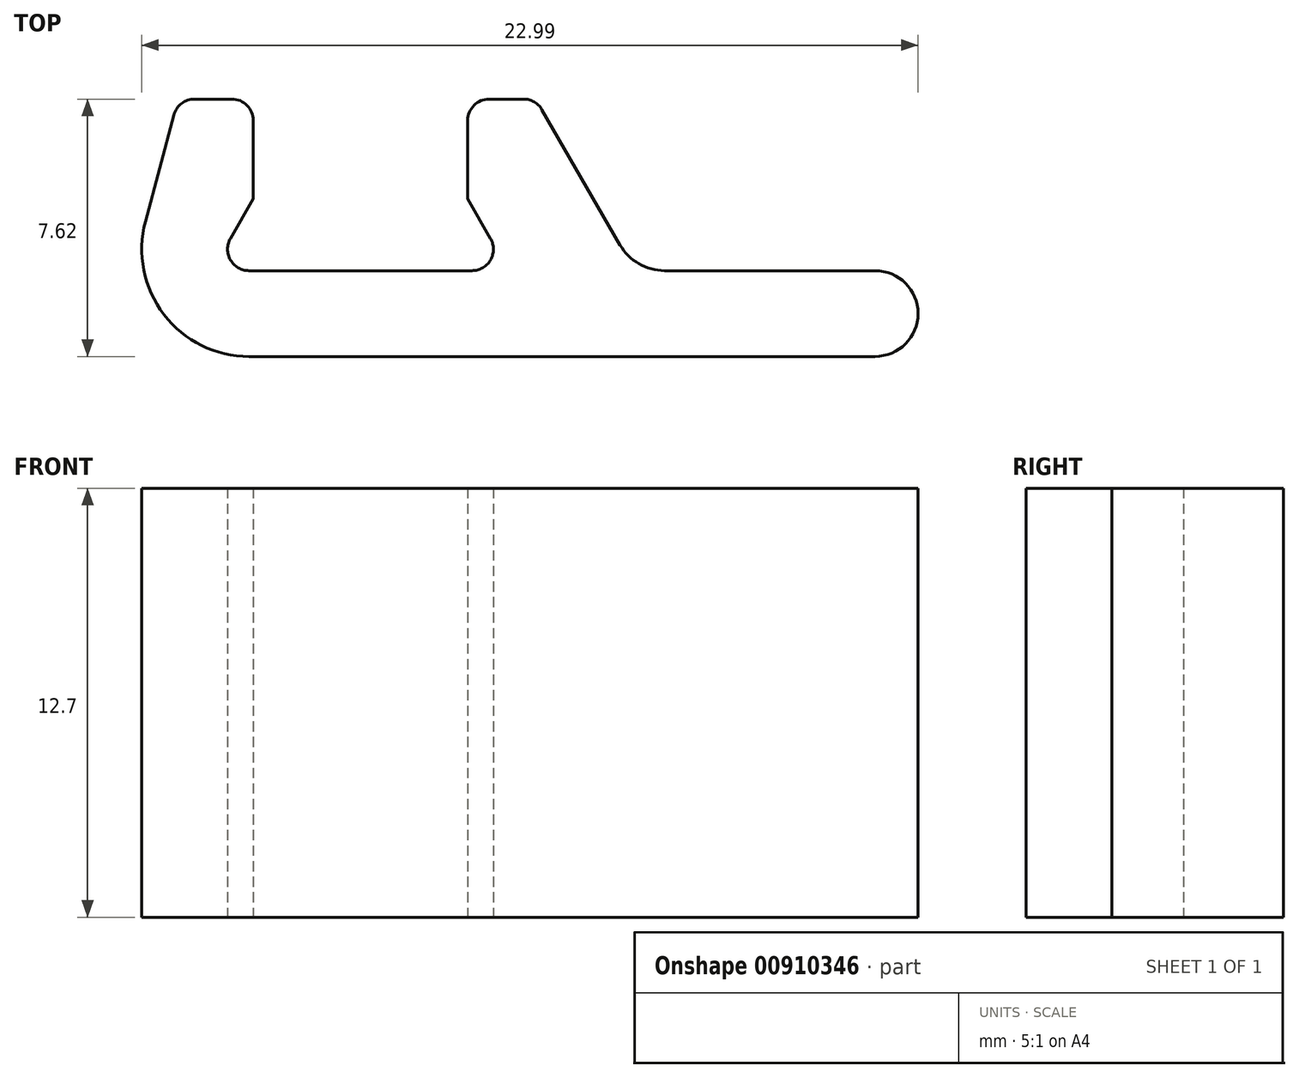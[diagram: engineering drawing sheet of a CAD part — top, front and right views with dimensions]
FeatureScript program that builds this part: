
annotation { "Feature Type Name" : "Feature", "Feature Type Description" : "" }
export const myFeature = defineFeature(function(context is Context, id is Id, definition is map)
    precondition{}
    {
        {
            var Q0;
            Q0=qCreatedBy(makeId("Top.planeOp"),FACE);
            var sketch = newSketch(context, id + "F0", { "sketchPlane" : qUnion([Q0])});
            skLineSegment(sketch, "E0", {"start": v(-3.3, 0) * mm, "end": v(3.3, 0) * mm});
            skLineSegment(sketch, "E1", {"start": v(-3.18, 2.12) * mm, "end": v(-3.18, 4.45) * mm});
            skLineSegment(sketch, "E2", {"start": v(-5.52, 4.6) * mm, "end": v(-6.37, 1.46) * mm});
            skLineSegment(sketch, "E3", {"start": v(3.18, 4.45) * mm, "end": v(3.18, 2.12) * mm});
            skLineSegment(sketch, "E4", {"start": v(-3.18, 2.12) * mm, "end": v(-3.85, 0.95) * mm});
            skLineSegment(sketch, "E5", {"start": v(3.18, 2.12) * mm, "end": v(3.85, 0.95) * mm});
            skArc(sketch, "E6", {"start": v(3.3, 0) * mm, "mid": v(3.85, 0.32) * mm, "end": v(3.85, 0.95) * mm});
            skArc(sketch, "E7", {"start": v(-3.85, 0.95) * mm, "mid": v(-3.85, 0.32) * mm, "end": v(-3.3, 0) * mm});
            skLineSegment(sketch, "E8", {"start": v(5.38, 4.76) * mm, "end": v(7.69, 0.76) * mm});
            skLineSegment(sketch, "E9", {"start": v(-4.91, 5.08) * mm, "end": v(-3.81, 5.08) * mm});
            skLineSegment(sketch, "E10", {"start": v(3.81, 5.08) * mm, "end": v(4.83, 5.08) * mm});
            skArc(sketch, "E11", {"start": v(-4.91, 5.08) * mm, "mid": v(-5.3, 4.95) * mm, "end": v(-5.52, 4.6) * mm});
            skArc(sketch, "E12", {"start": v(-3.18, 4.45) * mm, "mid": v(-3.36, 4.9) * mm, "end": v(-3.81, 5.08) * mm});
            skArc(sketch, "E13", {"start": v(3.81, 5.08) * mm, "mid": v(3.36, 4.9) * mm, "end": v(3.18, 4.45) * mm});
            skArc(sketch, "E14", {"start": v(5.38, 4.76) * mm, "mid": v(5.14, 5) * mm, "end": v(4.83, 5.08) * mm});
            skArc(sketch, "E15", {"start": v(-6.37, 1.46) * mm, "mid": v(-5.82, -1.3) * mm, "end": v(-3.3, -2.54) * mm});
            skLineSegment(sketch, "E16", {"start": v(-3.3, -2.54) * mm, "end": v(15.24, -2.54) * mm});
            skLineSegment(sketch, "E17", {"start": v(9, 0) * mm, "end": v(15.24, 0) * mm});
            skArc(sketch, "E18", {"start": v(15.24, -2.54) * mm, "mid": v(16.51, -1.27) * mm, "end": v(15.24, 0) * mm});
            skArc(sketch, "E19", {"start": v(7.69, 0.76) * mm, "mid": v(8.24, 0.2) * mm, "end": v(9, 0) * mm});
            skSolve(sketch);
        }
        {
            var Q0;
            Q0 = qSketchRegion(id + "F0", true);
            extrude(context, id + "F1", {"entities" : qUnion([Q0]), "depth" : 12.7 * mm, "offsetDistance" : 25.4 * mm});
        }
    });
